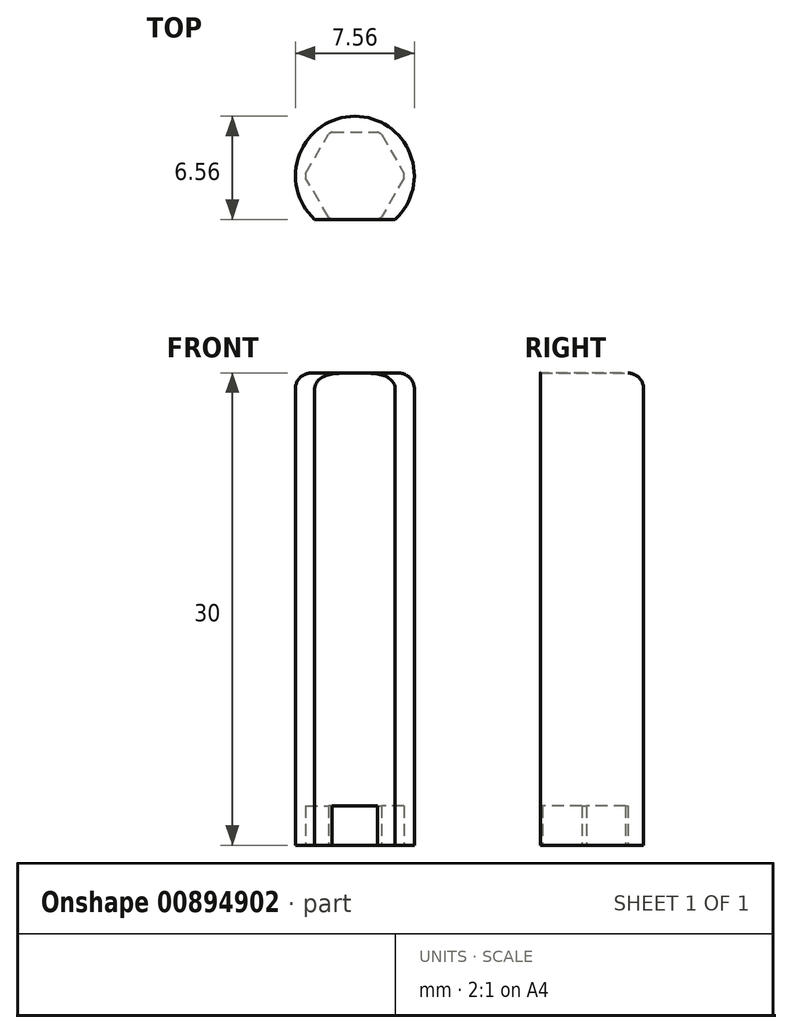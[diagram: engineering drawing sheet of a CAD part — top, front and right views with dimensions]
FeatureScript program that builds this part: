
annotation { "Feature Type Name" : "Feature", "Feature Type Description" : "" }
export const myFeature = defineFeature(function(context is Context, id is Id, definition is map)
    precondition{}
    {
        {
            var Q0;
            Q0=qCreatedBy(makeId("Top.planeOp"),FACE);
            var sketch = newSketch(context, id + "F0", { "sketchPlane" : qUnion([Q0])});
            skCircle(sketch, "E0.cCircle", {"center": v(0, 0) * mm, "radius": 2.78 * mm, "construction": true});
            skLineSegment(sketch, "E0.0", {"start": v(-1.6, 2.78) * mm, "end": v(1.6, 2.78) * mm});
            skLineSegment(sketch, "E0.1", {"start": v(1.6, 2.78) * mm, "end": v(3.2, 0) * mm});
            skLineSegment(sketch, "E0.2", {"start": v(3.2, 0) * mm, "end": v(1.6, -2.78) * mm});
            skLineSegment(sketch, "E0.3", {"start": v(2.56, -2.77) * mm, "end": v(-2.56, -2.78) * mm});
            skLineSegment(sketch, "E0.4", {"start": v(-1.6, -2.78) * mm, "end": v(-3.2, 0) * mm});
            skLineSegment(sketch, "E0.5", {"start": v(-3.2, 0) * mm, "end": v(-1.6, 2.78) * mm});
            skPoint(sketch, "E0.0.midPoint", {"position": v(0, 2.78) * mm});
            skCircle(sketch, "E1", {"center": v(0, 0) * mm, "radius": 3.12 * mm});
            skCircle(sketch, "E2", {"center": v(0, 0) * mm, "radius": 3.77 * mm});
            skSolve(sketch);
        }
        {
            var Q0;
            {var subQ1=sQuery(id+"F0.wireOp",EDGE,"E0.3");var subQ6=makeQuery(id+"F0.imprint","INTERSECT",VERTEX,{"derivedFrom":[sQuery(id+"F0.wireOp",EDGE,"E0.2"),subQ1]});Q0=makeQuery(id+"F0.imprint","IMPRINT",FACE,{"disambiguationData":[TD([[makeQuery(id+"F0.imprint","IMPRINT",EDGE,{"disambiguationData":[TD([[subQ6,1.0]])],"derivedFrom":subQ1}),1.0]])]});}
            var Q1;
            {var subQ10=sQuery(id+"F0.wireOp",EDGE,"E0.5");var subQ11=sQuery(id+"F0.wireOp",EDGE,"E0.0");var subQ12=makeQuery(id+"F0.imprint","INTERSECT",VERTEX,{"derivedFrom":[subQ11,subQ10]});Q1=makeQuery(id+"F0.imprint","IMPRINT",FACE,{"disambiguationData":[TD([[makeQuery(id+"F0.imprint","IMPRINT",EDGE,{"disambiguationData":[TD([[subQ12,-1.0]])],"derivedFrom":subQ11}),1.0]])]});}
            var Q2;
            {var subQ0=sQuery(id+"F0.wireOp",EDGE,"E1");var subQ1=sQuery(id+"F0.wireOp",EDGE,"E0.1");var subQ2=makeQuery(id+"F0.imprint","INTERSECT",VERTEX,{"disambiguationData":[OD(0.0)],"derivedFrom":[subQ1,subQ0]});Q2=makeQuery(id+"F0.imprint","IMPRINT",FACE,{"disambiguationData":[TD([[makeQuery(id+"F0.imprint","IMPRINT",EDGE,{"disambiguationData":[TD([[subQ2,-1.0]])],"derivedFrom":subQ1}),1.0]])]});}
            var Q3;
            {var subQ0=sQuery(id+"F0.wireOp",EDGE,"E1");var subQ1=sQuery(id+"F0.wireOp",EDGE,"E0.3");var subQ2=makeQuery(id+"F0.imprint","INTERSECT",VERTEX,{"disambiguationData":[OD(0.0)],"derivedFrom":[subQ1,subQ0]});Q3=makeQuery(id+"F0.imprint","IMPRINT",FACE,{"disambiguationData":[TD([[makeQuery(id+"F0.imprint","IMPRINT",EDGE,{"disambiguationData":[TD([[subQ2,-1.0]])],"derivedFrom":subQ1}),1.0]])]});}
            var Q4;
            {var subQ0=sQuery(id+"F0.wireOp",EDGE,"E1");var subQ1=sQuery(id+"F0.wireOp",EDGE,"E0.0");var subQ2=makeQuery(id+"F0.imprint","INTERSECT",VERTEX,{"disambiguationData":[OD(0.0)],"derivedFrom":[subQ1,subQ0]});Q4=makeQuery(id+"F0.imprint","IMPRINT",FACE,{"disambiguationData":[TD([[makeQuery(id+"F0.imprint","IMPRINT",EDGE,{"disambiguationData":[TD([[subQ2,-1.0]])],"derivedFrom":subQ1}),1.0]])]});}
            var Q5;
            {var subQ0=sQuery(id+"F0.wireOp",EDGE,"E1");var subQ1=sQuery(id+"F0.wireOp",EDGE,"E0.5");var subQ2=makeQuery(id+"F0.imprint","INTERSECT",VERTEX,{"disambiguationData":[OD(0.0)],"derivedFrom":[subQ1,subQ0]});Q5=makeQuery(id+"F0.imprint","IMPRINT",FACE,{"disambiguationData":[TD([[makeQuery(id+"F0.imprint","IMPRINT",EDGE,{"disambiguationData":[TD([[subQ2,-1.0]])],"derivedFrom":subQ1}),1.0]])]});}
            var Q6;
            {var subQ0=sQuery(id+"F0.wireOp",EDGE,"E1");var subQ11=sQuery(id+"F0.wireOp",EDGE,"E0.0");var subQ13=makeQuery(id+"F0.imprint","INTERSECT",VERTEX,{"disambiguationData":[OD(0.0)],"derivedFrom":[subQ11,subQ0]});Q6=makeQuery(id+"F0.imprint","IMPRINT",FACE,{"disambiguationData":[TD([[makeQuery(id+"F0.imprint","IMPRINT",EDGE,{"disambiguationData":[TD([[subQ13,-1.0]])],"derivedFrom":subQ11}),-1.0]])]});}
            var Q7;
            {var subQ0=sQuery(id+"F0.wireOp",EDGE,"E1");var subQ1=sQuery(id+"F0.wireOp",EDGE,"E0.4");var subQ2=makeQuery(id+"F0.imprint","INTERSECT",VERTEX,{"disambiguationData":[OD(0.0)],"derivedFrom":[subQ1,subQ0]});Q7=makeQuery(id+"F0.imprint","IMPRINT",FACE,{"disambiguationData":[TD([[makeQuery(id+"F0.imprint","IMPRINT",EDGE,{"disambiguationData":[TD([[subQ2,-1.0]])],"derivedFrom":subQ1}),1.0]])]});}
            var Q8;
            {var subQ0=sQuery(id+"F0.wireOp",EDGE,"E1");var subQ1=sQuery(id+"F0.wireOp",EDGE,"E0.2");var subQ2=makeQuery(id+"F0.imprint","INTERSECT",VERTEX,{"disambiguationData":[OD(0.0)],"derivedFrom":[subQ1,subQ0]});Q8=makeQuery(id+"F0.imprint","IMPRINT",FACE,{"disambiguationData":[TD([[makeQuery(id+"F0.imprint","IMPRINT",EDGE,{"disambiguationData":[TD([[subQ2,-1.0]])],"derivedFrom":subQ1}),1.0]])]});}
            var Q9;
            {var subQ0=sQuery(id+"F0.wireOp",EDGE,"E0.4");var subQ1=sQuery(id+"F0.wireOp",EDGE,"E0.3");var subQ2=makeQuery(id+"F0.imprint","INTERSECT",VERTEX,{"derivedFrom":[subQ1,subQ0]});Q9=makeQuery(id+"F0.imprint","IMPRINT",FACE,{"disambiguationData":[TD([[makeQuery(id+"F0.imprint","IMPRINT",EDGE,{"disambiguationData":[TD([[subQ2,1.0]])],"derivedFrom":subQ1}),-1.0]])]});}
            var Q10;
            {var subQ0=sQuery(id+"F0.wireOp",EDGE,"E0.3");var subQ1=sQuery(id+"F0.wireOp",EDGE,"E0.2");var subQ2=makeQuery(id+"F0.imprint","INTERSECT",VERTEX,{"derivedFrom":[subQ1,subQ0]});Q10=makeQuery(id+"F0.imprint","IMPRINT",FACE,{"disambiguationData":[TD([[makeQuery(id+"F0.imprint","IMPRINT",EDGE,{"disambiguationData":[TD([[subQ2,1.0]])],"derivedFrom":subQ1}),-1.0]])]});}
            var Q11;
            {var subQ0=sQuery(id+"F0.wireOp",EDGE,"E0.2");var subQ1=sQuery(id+"F0.wireOp",EDGE,"E0.1");var subQ2=makeQuery(id+"F0.imprint","INTERSECT",VERTEX,{"derivedFrom":[subQ1,subQ0]});Q11=makeQuery(id+"F0.imprint","IMPRINT",FACE,{"disambiguationData":[TD([[makeQuery(id+"F0.imprint","IMPRINT",EDGE,{"disambiguationData":[TD([[subQ2,1.0]])],"derivedFrom":subQ1}),-1.0]])]});}
            var Q12;
            {var subQ0=sQuery(id+"F0.wireOp",EDGE,"E0.5");var subQ1=sQuery(id+"F0.wireOp",EDGE,"E0.4");var subQ2=makeQuery(id+"F0.imprint","INTERSECT",VERTEX,{"derivedFrom":[subQ1,subQ0]});Q12=makeQuery(id+"F0.imprint","IMPRINT",FACE,{"disambiguationData":[TD([[makeQuery(id+"F0.imprint","IMPRINT",EDGE,{"disambiguationData":[TD([[subQ2,1.0]])],"derivedFrom":subQ1}),-1.0]])]});}
            var Q13;
            {var subQ0=sQuery(id+"F0.wireOp",EDGE,"E0.1");var subQ1=sQuery(id+"F0.wireOp",EDGE,"E0.0");var subQ2=makeQuery(id+"F0.imprint","INTERSECT",VERTEX,{"derivedFrom":[subQ1,subQ0]});Q13=makeQuery(id+"F0.imprint","IMPRINT",FACE,{"disambiguationData":[TD([[makeQuery(id+"F0.imprint","IMPRINT",EDGE,{"disambiguationData":[TD([[subQ2,1.0]])],"derivedFrom":subQ1}),-1.0]])]});}
            var Q14;
            {var subQ0=sQuery(id+"F0.wireOp",EDGE,"E0.5");var subQ1=sQuery(id+"F0.wireOp",EDGE,"E0.0");var subQ2=makeQuery(id+"F0.imprint","INTERSECT",VERTEX,{"derivedFrom":[subQ1,subQ0]});Q14=makeQuery(id+"F0.imprint","IMPRINT",FACE,{"disambiguationData":[TD([[makeQuery(id+"F0.imprint","IMPRINT",EDGE,{"disambiguationData":[TD([[subQ2,-1.0]])],"derivedFrom":subQ1}),-1.0]])]});}
            extrude(context, id + "F1", {"entities" : qUnion([Q0, Q1, Q2, Q3, Q4, Q5, Q6, Q7, Q8, Q9, Q10, Q11, Q12, Q13, Q14]), "depth" : 30 * mm, "offsetDistance" : 25 * mm});
        }
        {
            var Q0;
            {var subQ0=sQuery(id+"F0.wireOp",EDGE,"E1");var subQ11=sQuery(id+"F0.wireOp",EDGE,"E0.0");var subQ13=makeQuery(id+"F0.imprint","INTERSECT",VERTEX,{"disambiguationData":[OD(0.0)],"derivedFrom":[subQ11,subQ0]});Q0=makeQuery(id+"F0.imprint","IMPRINT",FACE,{"disambiguationData":[TD([[makeQuery(id+"F0.imprint","IMPRINT",EDGE,{"disambiguationData":[TD([[subQ13,-1.0]])],"derivedFrom":subQ11}),-1.0]])]});}
            extrude(context, id + "F2", {"entities" : qUnion([Q0]), "operationType" : NewBodyOperationType.REMOVE, "depth" : 2.5 * mm, "offsetDistance" : 25 * mm});
        }
        {
            var Q0;
            {var subQ0=sQuery(id+"F0.wireOp",EDGE,"E1");var subQ1=sQuery(id+"F0.wireOp",EDGE,"E0.3");var subQ2=makeQuery(id+"F0.imprint","INTERSECT",VERTEX,{"disambiguationData":[OD(0.0)],"derivedFrom":[subQ1,subQ0]});Q0=makeQuery(id+"F0.imprint","IMPRINT",FACE,{"disambiguationData":[TD([[makeQuery(id+"F0.imprint","IMPRINT",EDGE,{"disambiguationData":[TD([[subQ2,-1.0]])],"derivedFrom":subQ1}),1.0]])]});}
            var Q1;
            {var subQ1=sQuery(id+"F0.wireOp",EDGE,"E0.3");var subQ6=makeQuery(id+"F0.imprint","INTERSECT",VERTEX,{"derivedFrom":[sQuery(id+"F0.wireOp",EDGE,"E0.2"),subQ1]});Q1=makeQuery(id+"F0.imprint","IMPRINT",FACE,{"disambiguationData":[TD([[makeQuery(id+"F0.imprint","IMPRINT",EDGE,{"disambiguationData":[TD([[subQ6,1.0]])],"derivedFrom":subQ1}),1.0]])]});}
            var Q2;
            Q2=makeQuery(id+"F1.opExtrude","CAP_FACE",FACE,{"disambiguationData":[OSD([sQuery(id+"F0.wireOp",EDGE,"E2")])],"isStart":false});
            extrude(context, id + "F3", {"entities" : qUnion([Q0, Q1]), "operationType" : NewBodyOperationType.REMOVE, "endBound" : BoundingType.UP_TO_SURFACE, "depth" : 25 * mm, "endBoundEntityFace" : qUnion([Q2]), "offsetDistance" : 25 * mm});
        }
        {
            var Q0;
            Q0=makeQuery(id+"F1.opExtrude","CAP_EDGE",EDGE,{"disambiguationData":[OSD([sQuery(id+"F0.wireOp",EDGE,"E2")])],"isStart":false});
            var Q1;
            Q1=makeQuery(id+"F3.boolean.opBoolean","COPY",EDGE,{"derivedFrom":makeQuery(id+"F3.opExtrude","CAP_EDGE",EDGE,{"disambiguationData":[OSD([sQuery(id+"F0.wireOp",EDGE,"E0.3")])],"isStart":false})});
            fillet(context, id + "F4", {"entities" : qUnion([Q0, Q1]), "radius" : 1 * mm, "tangentPropagation" : true, "allowEdgeOverflow" : false});
        }
    });
